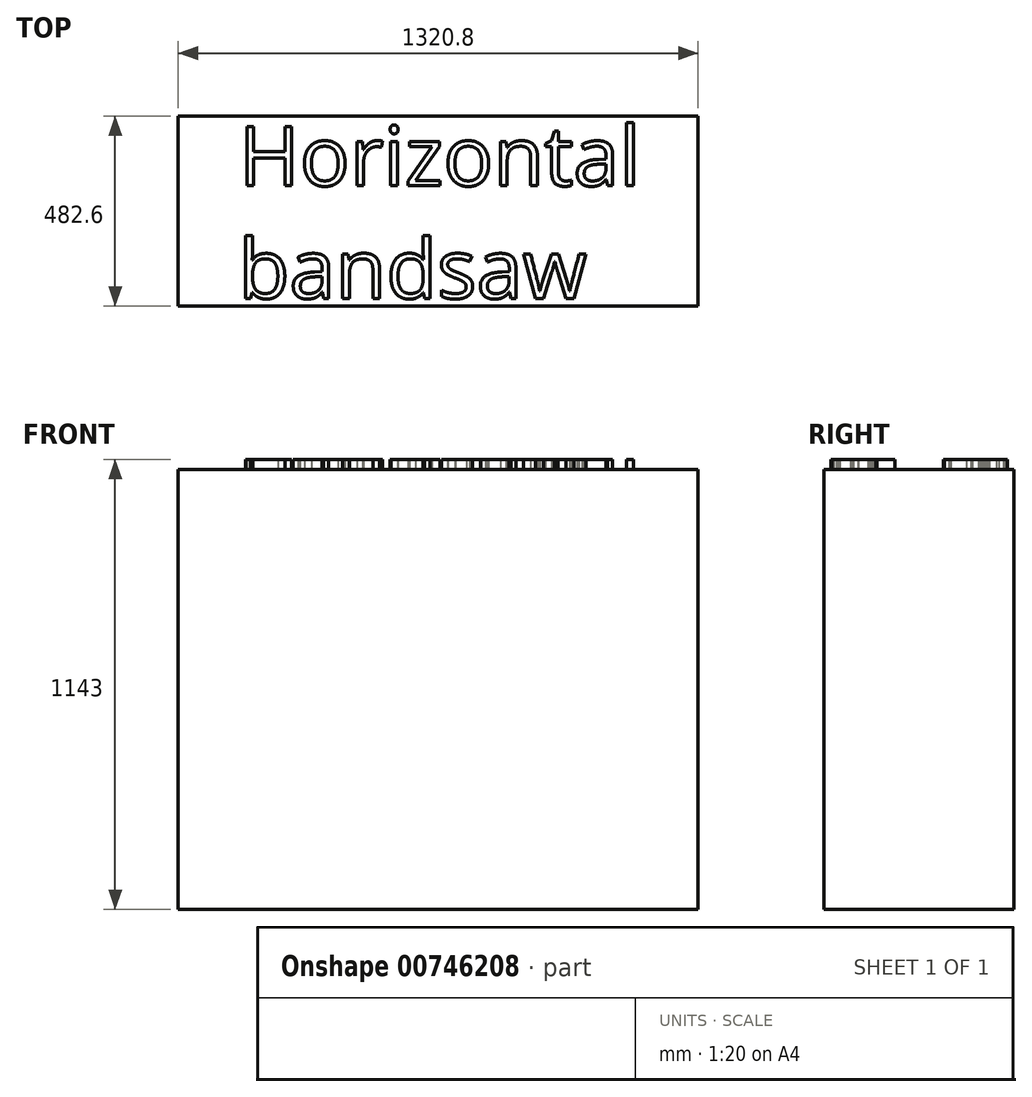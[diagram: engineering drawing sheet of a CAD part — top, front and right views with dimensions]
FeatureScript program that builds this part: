
annotation { "Feature Type Name" : "Feature", "Feature Type Description" : "" }
export const myFeature = defineFeature(function(context is Context, id is Id, definition is map)
    precondition{}
    {
        {
            var Q0;
            Q0=qCreatedBy(makeId("Top.planeOp"),FACE);
            var sketch = newSketch(context, id + "F0", { "sketchPlane" : qUnion([Q0])});
            skLineSegment(sketch, "E0.bottom", {"start": v(659.14, -241.3) * mm, "end": v(-661.66, -241.3) * mm});
            skLineSegment(sketch, "E0.top", {"start": v(659.14, 241.3) * mm, "end": v(-661.66, 241.3) * mm});
            skLineSegment(sketch, "E0.left", {"start": v(659.14, -241.3) * mm, "end": v(659.14, 241.3) * mm});
            skLineSegment(sketch, "E0.right", {"start": v(-661.66, -241.3) * mm, "end": v(-661.66, 241.3) * mm});
            skPoint(sketch, "E0.middle", {"position": v(-1.26, 0) * mm});
            skSolve(sketch);
        }
        {
            var Q0;
            Q0 = qSketchRegion(id + "F0", true);
            extrude(context, id + "F1", {"entities" : qUnion([Q0]), "depth" : 1117.6 * mm, "offsetDistance" : 25.4 * mm});
        }
        {
            var Q0;
            Q0=makeQuery(id+"F1.opExtrude","CAP_FACE",FACE,{"disambiguationData":[OSD([sQuery(id+"F0.wireOp",EDGE,"E0.bottom"),sQuery(id+"F0.wireOp",EDGE,"E0.top"),sQuery(id+"F0.wireOp",EDGE,"E0.left"),sQuery(id+"F0.wireOp",EDGE,"E0.right")])],"isStart":false});
            var sketch = newSketch(context, id + "F2", { "sketchPlane" : qUnion([Q0])});
            skText(sketch, "E1", { "text": "Horizontal \nbandsaw", "fontName": "OpenSans-Regular.ttf"});
            const initialGuessF2  = {"E1": [-0.508, 0.06444, 1, 0, 0.15146]};
            skSetInitialGuess(sketch, initialGuessF2);
            skSolve(sketch);
        }
        {
            var Q0;
            Q0 = qSketchRegion(id + "F2", true);
            extrude(context, id + "F3", {"entities" : qUnion([Q0]), "operationType" : NewBodyOperationType.ADD, "depth" : 25.4 * mm, "offsetDistance" : 25.4 * mm});
        }
    });
